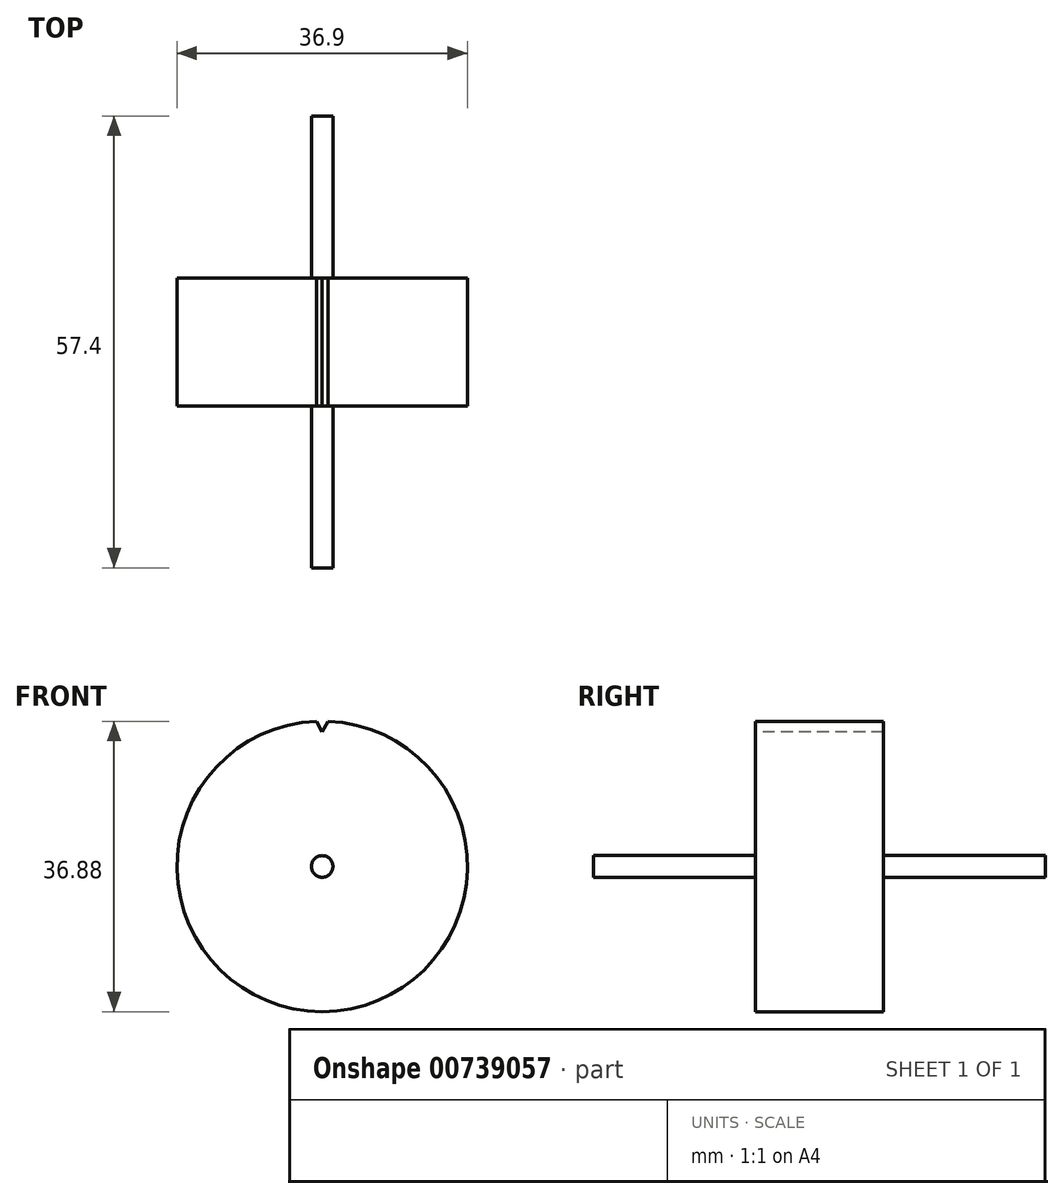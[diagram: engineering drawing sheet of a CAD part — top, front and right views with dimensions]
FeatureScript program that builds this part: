
annotation { "Feature Type Name" : "Feature", "Feature Type Description" : "" }
export const myFeature = defineFeature(function(context is Context, id is Id, definition is map)
    precondition{}
    {
        {
            var Q0;
            Q0=qCreatedBy(makeId("Front.planeOp"),FACE);
            var sketch = newSketch(context, id + "F0", { "sketchPlane" : qUnion([Q0])});
            skCircle(sketch, "E0", {"center": v(0, 0) * mm, "radius": 18.45 * mm});
            skSolve(sketch);
        }
        {
            var Q0;
            Q0 = qSketchRegion(id + "F0", true);
            extrude(context, id + "F1", {"entities" : qUnion([Q0]), "endBound" : BoundingType.SYMMETRIC, "depth" : 16.26 * mm, "offsetDistance" : 25.4 * mm});
        }
        {
            var Q0;
            Q0=qCreatedBy(makeId("Right.planeOp"),FACE);
            var sketch = newSketch(context, id + "F2", { "sketchPlane" : qUnion([Q0])});
            skLineSegment(sketch, "E1", {"start": v(-8.16, 0) * mm, "end": v(8.24, 0) * mm});
            skSolve(sketch);
        }
        {
            var Q0;
            Q0=qCreatedBy(makeId("Right.planeOp"),FACE);
            var sketch = newSketch(context, id + "F3", { "sketchPlane" : qUnion([Q0])});
            skLineSegment(sketch, "E2", {"start": v(-8.13, 18.45) * mm, "end": v(8.14, 18.45) * mm});
            skSolve(sketch);
        }
        {
            var Q0;
            Q0=qCreatedBy(makeId("Front.planeOp"),FACE);
            var sketch = newSketch(context, id + "F4", { "sketchPlane" : qUnion([Q0])});
            skLineSegment(sketch, "E3", {"start": v(0, 18.47) * mm, "end": v(0.75, 18.47) * mm});
            skLineSegment(sketch, "E4", {"start": v(0.75, 18.47) * mm, "end": v(0, 17.08) * mm});
            skLineSegment(sketch, "E5", {"start": v(0, 17.08) * mm, "end": v(0, 18.47) * mm});
            skLineSegment(sketch, "E6.MirrorCS", {"start": v(-0.75, 18.47) * mm, "end": v(0, 17.08) * mm});
            skLineSegment(sketch, "E7.MirrorCS", {"start": v(0, 18.47) * mm, "end": v(-0.75, 18.47) * mm});
            skSolve(sketch);
        }
        {
            var Q0;
            Q0=makeQuery(id+"F4.imprint","IMPRINT",FACE,{"disambiguationData":[TD([[makeQuery(id+"F4.imprint","IMPRINT",EDGE,{"derivedFrom":sQuery(id+"F4.wireOp",EDGE,"E3")}),-1.0]])]});
            var Q1;
            Q1=makeQuery(id+"F4.imprint","IMPRINT",FACE,{"disambiguationData":[TD([[makeQuery(id+"F4.imprint","IMPRINT",EDGE,{"derivedFrom":sQuery(id+"F4.wireOp",EDGE,"E5")}),1.0]])]});
            var Q2;
            Q2=sQuery(id+"F3.wireOp",EDGE,"E2");
            sweep(context, id + "F5", {"operationType" : NewBodyOperationType.REMOVE, "profiles" : qUnion([Q0, Q1]), "path" : qUnion([Q2])});
        }
        {
            var Q0;
            Q0=qCreatedBy(makeId("Front.planeOp"),FACE);
            var sketch = newSketch(context, id + "F6", { "sketchPlane" : qUnion([Q0])});
            skCircle(sketch, "E8", {"center": v(0, 0) * mm, "radius": 1.37 * mm});
            skSolve(sketch);
        }
        {
            var Q0;
            Q0 = qSketchRegion(id + "F6", true);
            extrude(context, id + "F7", {"entities" : qUnion([Q0]), "operationType" : NewBodyOperationType.ADD, "endBound" : BoundingType.SYMMETRIC, "depth" : 57.4 * mm, "offsetDistance" : 25.4 * mm});
        }
    });
